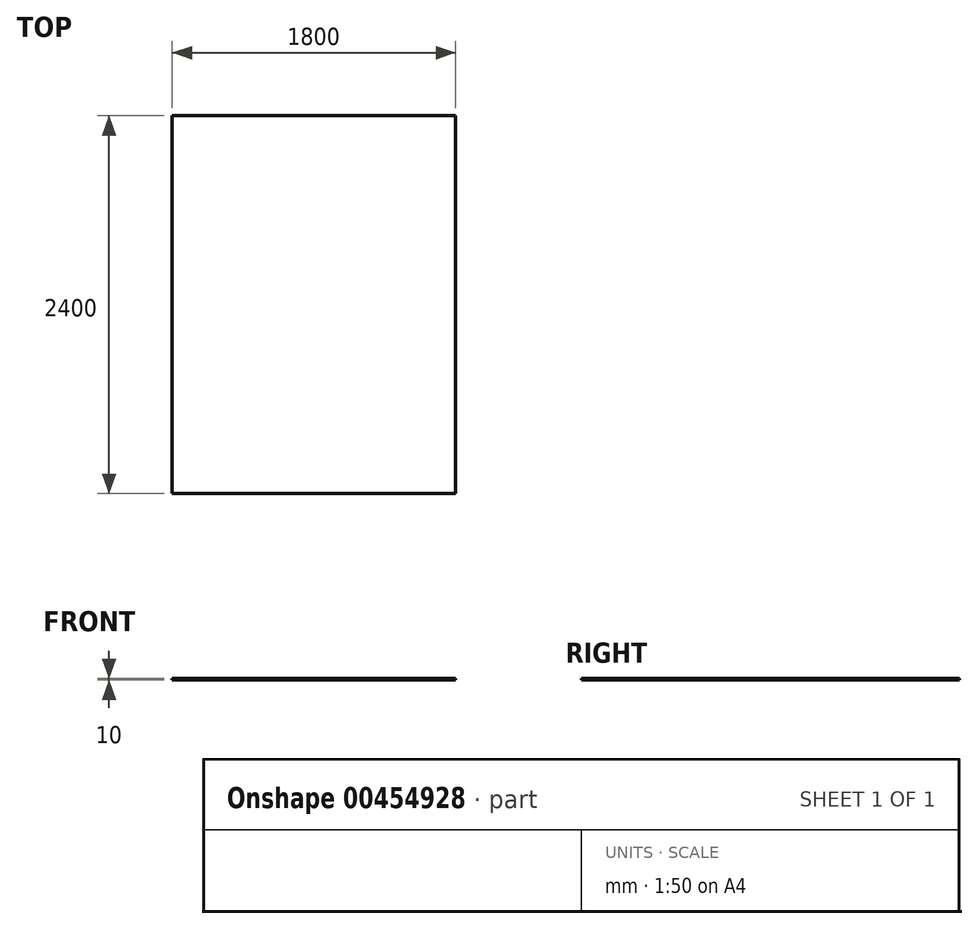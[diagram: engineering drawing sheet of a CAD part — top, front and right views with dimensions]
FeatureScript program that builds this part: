
annotation { "Feature Type Name" : "Feature", "Feature Type Description" : "" }
export const myFeature = defineFeature(function(context is Context, id is Id, definition is map)
    precondition{}
    {
        {
            var Q0;
            Q0=qCreatedBy(makeId("Top.planeOp"),FACE);
            var sketch = newSketch(context, id + "F0", { "sketchPlane" : qUnion([Q0])});
            skLineSegment(sketch, "E0.bottom", {"start": v(0, 2400) * mm, "end": v(1800, 2400) * mm});
            skLineSegment(sketch, "E0.top", {"start": v(0, 0) * mm, "end": v(1800, 0) * mm});
            skLineSegment(sketch, "E0.left", {"start": v(0, 2400) * mm, "end": v(0, 0) * mm});
            skLineSegment(sketch, "E0.right", {"start": v(1800, 2400) * mm, "end": v(1800, 0) * mm});
            skSolve(sketch);
        }
        {
            var Q0;
            Q0 = qSketchRegion(id + "F0", true);
            extrude(context, id + "F1", {"entities" : qUnion([Q0]), "depth" : -10 * mm});
        }
    });
